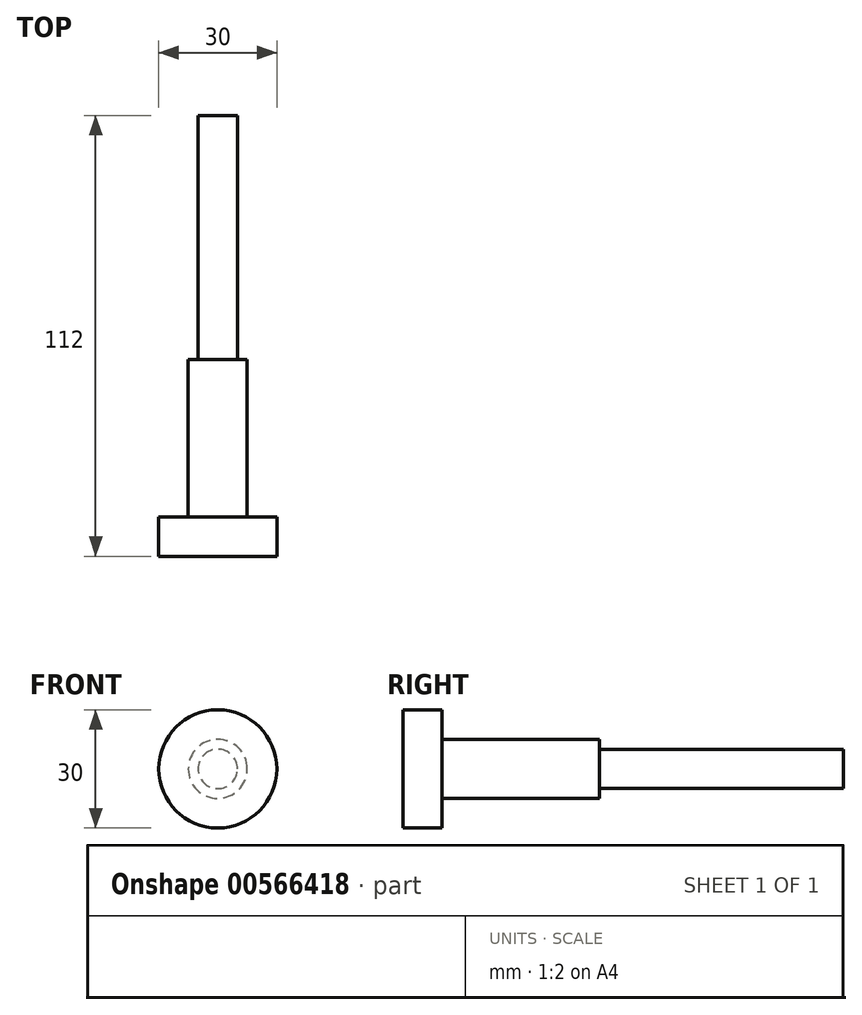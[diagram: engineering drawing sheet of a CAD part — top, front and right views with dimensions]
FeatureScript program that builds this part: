
annotation { "Feature Type Name" : "Feature", "Feature Type Description" : "" }
export const myFeature = defineFeature(function(context is Context, id is Id, definition is map)
    precondition{}
    {
        {
            var Q0;
            Q0=qCreatedBy(makeId("Front.planeOp"),FACE);
            var sketch = newSketch(context, id + "F0", { "sketchPlane" : qUnion([Q0])});
            skCircle(sketch, "E0", {"center": v(0, 0) * mm, "radius": 15 * mm});
            skSolve(sketch);
        }
        {
            var Q0;
            Q0=makeQuery(id+"F0.imprint","IMPRINT",FACE,{"disambiguationData":[TD([[makeQuery(id+"F0.imprint","IMPRINT",EDGE,{"derivedFrom":sQuery(id+"F0.wireOp",EDGE,"E0")}),1.0]])]});
            extrude(context, id + "F1", {"entities" : qUnion([Q0]), "depth" : 112 * mm, "offsetDistance" : 25 * mm});
        }
        {
            var Q0;
            Q0=qCreatedBy(makeId("Front.planeOp"),FACE);
            var sketch = newSketch(context, id + "F2", { "sketchPlane" : qUnion([Q0])});
            skCircle(sketch, "E1", {"center": v(0, 0) * mm, "radius": 7.5 * mm});
            skCircle(sketch, "E2", {"center": v(0, 0) * mm, "radius": 15 * mm});
            skSolve(sketch);
        }
        {
            var Q0;
            Q0 = qSketchRegion(id + "F2", true);
            extrude(context, id + "F3", {"entities" : qUnion([Q0]), "operationType" : NewBodyOperationType.REMOVE, "depth" : 102 * mm, "offsetDistance" : 25 * mm});
        }
        {
            var Q0;
            Q0=makeQuery(id+"F1.opExtrude","CAP_FACE",FACE,{"disambiguationData":[OSD([sQuery(id+"F0.wireOp",EDGE,"E0")])],"isStart":true});
            var sketch = newSketch(context, id + "F4", { "sketchPlane" : qUnion([Q0])});
            skCircle(sketch, "E3", {"center": v(0, 0) * mm, "radius": 5 * mm});
            skCircle(sketch, "E4", {"center": v(0, 0) * mm, "radius": 7.5 * mm});
            skSolve(sketch);
        }
        {
            var Q0;
            Q0 = qSketchRegion(id + "F4", true);
            extrude(context, id + "F5", {"entities" : qUnion([Q0]), "operationType" : NewBodyOperationType.REMOVE, "oppositeDirection" : true, "depth" : 62 * mm, "offsetDistance" : 25 * mm});
        }
    });
